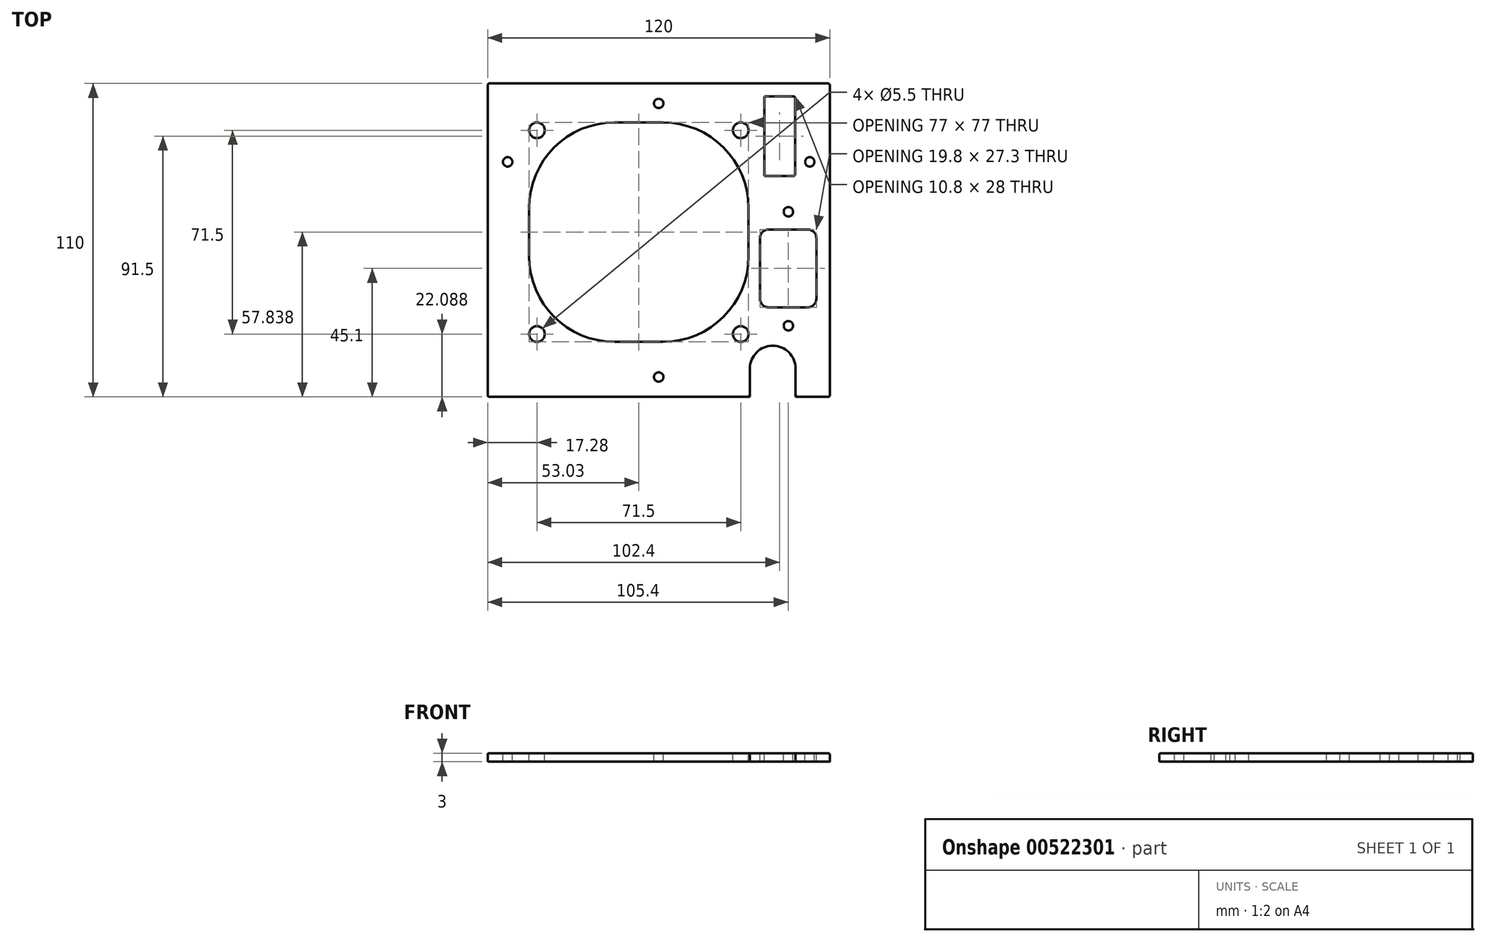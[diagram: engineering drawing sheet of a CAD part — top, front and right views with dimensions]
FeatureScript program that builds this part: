
annotation { "Feature Type Name" : "Feature", "Feature Type Description" : "" }
export const myFeature = defineFeature(function(context is Context, id is Id, definition is map)
    precondition{}
    {
        {
            var Q0;
            Q0=qCreatedBy(makeId("Top.planeOp"),FACE);
            var sketch = newSketch(context, id + "F0", { "sketchPlane" : qUnion([Q0])});
            skLineSegment(sketch, "E0.bottom", {"start": v(-60, 55) * mm, "end": v(60, 55) * mm});
            skLineSegment(sketch, "E0.top", {"start": v(-60, -55) * mm, "end": v(32, -55) * mm});
            skLineSegment(sketch, "E0.left", {"start": v(-60, 55) * mm, "end": v(-60, -55) * mm});
            skLineSegment(sketch, "E0.right", {"start": v(60, 55) * mm, "end": v(60, -55) * mm});
            skArc(sketch, "E1", {"start": v(48, -45) * mm, "mid": v(40, -37) * mm, "end": v(32, -45) * mm});
            skLineSegment(sketch, "E2", {"start": v(48, -45) * mm, "end": v(48, -55) * mm});
            skLineSegment(sketch, "E3", {"start": v(32, -45) * mm, "end": v(32, -55) * mm});
            skLineSegment(sketch, "E4.trimOffspring", {"start": v(48, -55) * mm, "end": v(60, -55) * mm});
            skSolve(sketch);
        }
        {
            var Q0;
            Q0=makeQuery(id+"F0.imprint","IMPRINT",FACE,{"disambiguationData":[TD([[makeQuery(id+"F0.imprint","IMPRINT",EDGE,{"derivedFrom":sQuery(id+"F0.wireOp",EDGE,"E0.bottom")}),-1.0]])]});
            var Q1;
            Q1 = qSketchRegion(id + "F2", true);
            extrude(context, id + "F1", {"entities" : qUnion([Q0, Q1]), "depth" : 3 * mm, "offsetDistance" : 25 * mm});
        }
        {
            var Q0;
            Q0=makeQuery(id+"F1.opExtrude","CAP_FACE",FACE,{"disambiguationData":[OSD([sQuery(id+"F0.wireOp",EDGE,"E0.bottom"),sQuery(id+"F0.wireOp",EDGE,"E0.top"),sQuery(id+"F0.wireOp",EDGE,"E0.left"),sQuery(id+"F0.wireOp",EDGE,"E0.right"),sQuery(id+"F0.wireOp",EDGE,"E1"),sQuery(id+"F0.wireOp",EDGE,"E2"),sQuery(id+"F0.wireOp",EDGE,"E3"),sQuery(id+"F0.wireOp",EDGE,"E4.trimOffspring")])],"isStart":false});
            var sketch = newSketch(context, id + "F2", { "sketchPlane" : qUnion([Q0])});
            skPoint(sketch, "E5", {"position": v(-53, 27.5) * mm});
            skPoint(sketch, "E6", {"position": v(53, 27.5) * mm});
            skPoint(sketch, "E7", {"position": v(0, 48) * mm});
            skPoint(sketch, "E8", {"position": v(0, -48) * mm});
            skSolve(sketch);
        }
        {
            var Q0;
            Q0=sQuery(id+"F2.wireOp",VERTEX,"E5");
            var Q1;
            Q1=sQuery(id+"F2.wireOp",VERTEX,"E7");
            var Q2;
            Q2=sQuery(id+"F2.wireOp",VERTEX,"E6");
            var Q3;
            Q3=sQuery(id+"F2.wireOp",VERTEX,"E8");
            var Q4;
            Q4=makeQuery(id+"F1.opExtrude","SWEPT_BODY",BODY,{"disambiguationData":[OSD([sQuery(id+"F0.wireOp",EDGE,"E0.bottom"),sQuery(id+"F0.wireOp",EDGE,"E0.top"),sQuery(id+"F0.wireOp",EDGE,"E0.left"),sQuery(id+"F0.wireOp",EDGE,"E0.right"),sQuery(id+"F0.wireOp",EDGE,"E1"),sQuery(id+"F0.wireOp",EDGE,"E2"),sQuery(id+"F0.wireOp",EDGE,"E3"),sQuery(id+"F0.wireOp",EDGE,"E4.trimOffspring")])]});
            hole(context, id + "F3", {"style" : HoleStyle.SIMPLE, "endStyle" : HoleEndStyle.THROUGH, "standardTappedOrClearance" : lookupTablePath({ "standard" : "ISO", "fit" : "Normal", "size" : "M3", "type" : "Clearance" }), "standardBlindInLast" : lookupTablePath({ "fit" : "Standard", "standard" : "ISO", "size" : "M3", "type" : "Clearance" }), "holeDiameter" : 3.3 * mm, "isTappedThrough" : true, "tappedDepth" : 12 * mm, "tapClearance" : 3, "locations" : qUnion([Q0, Q1, Q2, Q3]), "scope" : qUnion([Q4])});
        }
        {
            var Q0;
            Q0=makeQuery(id+"F1.opExtrude","CAP_FACE",FACE,{"disambiguationData":[OSD([sQuery(id+"F0.wireOp",EDGE,"E0.bottom"),sQuery(id+"F0.wireOp",EDGE,"E0.top"),sQuery(id+"F0.wireOp",EDGE,"E0.left"),sQuery(id+"F0.wireOp",EDGE,"E0.right"),sQuery(id+"F0.wireOp",EDGE,"E1"),sQuery(id+"F0.wireOp",EDGE,"E2"),sQuery(id+"F0.wireOp",EDGE,"E3"),sQuery(id+"F0.wireOp",EDGE,"E4.trimOffspring")])],"isStart":false});
            var sketch = newSketch(context, id + "F4", { "sketchPlane" : qUnion([Q0])});
            skPoint(sketch, "E9", {"position": v(-42.72, 38.59) * mm});
            skPoint(sketch, "E10", {"position": v(-42.72, -32.91) * mm});
            skPoint(sketch, "E11", {"position": v(28.78, -32.91) * mm});
            skPoint(sketch, "E12", {"position": v(28.78, 38.59) * mm});
            skLineSegment(sketch, "E13.bottom", {"start": v(1.53, 41.34) * mm, "end": v(-15.47, 41.34) * mm});
            skLineSegment(sketch, "E13.top", {"start": v(1.53, -35.66) * mm, "end": v(-15.47, -35.66) * mm});
            skLineSegment(sketch, "E13.left", {"start": v(31.53, 11.34) * mm, "end": v(31.53, -5.66) * mm});
            skLineSegment(sketch, "E13.right", {"start": v(-45.47, 11.34) * mm, "end": v(-45.47, -5.66) * mm});
            skPoint(sketch, "E14.visualSharp", {"position": v(-45.47, 41.34) * mm});
            skArc(sketch, "E14.filletArc", {"start": v(-15.47, 41.34) * mm, "mid": v(-36.68, 32.55) * mm, "end": v(-45.47, 11.34) * mm});
            skPoint(sketch, "E15.visualSharp", {"position": v(31.53, 41.34) * mm});
            skArc(sketch, "E15.filletArc", {"start": v(31.53, 11.34) * mm, "mid": v(22.74, 32.55) * mm, "end": v(1.53, 41.34) * mm});
            skPoint(sketch, "E16.visualSharp", {"position": v(31.53, -35.66) * mm});
            skArc(sketch, "E16.filletArc", {"start": v(1.53, -35.66) * mm, "mid": v(22.74, -26.88) * mm, "end": v(31.53, -5.66) * mm});
            skPoint(sketch, "E17.visualSharp", {"position": v(-45.47, -35.66) * mm});
            skArc(sketch, "E17.filletArc", {"start": v(-45.47, -5.66) * mm, "mid": v(-36.68, -26.88) * mm, "end": v(-15.47, -35.66) * mm});
            skSolve(sketch);
        }
        {
            var Q0;
            Q0=sQuery(id+"F4.wireOp",VERTEX,"E9");
            var Q1;
            Q1=sQuery(id+"F4.wireOp",VERTEX,"E10");
            var Q2;
            Q2=sQuery(id+"F4.wireOp",VERTEX,"E11");
            var Q3;
            Q3=sQuery(id+"F4.wireOp",VERTEX,"E12");
            var Q4;
            Q4=makeQuery(id+"F1.opExtrude","SWEPT_BODY",BODY,{"disambiguationData":[OSD([sQuery(id+"F0.wireOp",EDGE,"E0.bottom"),sQuery(id+"F0.wireOp",EDGE,"E0.top"),sQuery(id+"F0.wireOp",EDGE,"E0.left"),sQuery(id+"F0.wireOp",EDGE,"E0.right"),sQuery(id+"F0.wireOp",EDGE,"E1"),sQuery(id+"F0.wireOp",EDGE,"E2"),sQuery(id+"F0.wireOp",EDGE,"E3"),sQuery(id+"F0.wireOp",EDGE,"E4.trimOffspring")])]});
            hole(context, id + "F5", {"style" : HoleStyle.SIMPLE, "endStyle" : HoleEndStyle.THROUGH, "standardTappedOrClearance" : lookupTablePath({ "standard" : "ISO", "fit" : "Normal", "size" : "M5", "type" : "Clearance" }), "standardBlindInLast" : lookupTablePath({ "fit" : "Standard", "standard" : "ISO", "size" : "M5", "type" : "Clearance" }), "holeDiameter" : 5.5 * mm, "isTappedThrough" : true, "tappedDepth" : 12 * mm, "tapClearance" : 3, "locations" : qUnion([Q0, Q1, Q2, Q3]), "scope" : qUnion([Q4])});
        }
        {
            var Q0;
            Q0 = qSketchRegion(id + "F4", true);
            extrude(context, id + "F6", {"entities" : qUnion([Q0]), "operationType" : NewBodyOperationType.REMOVE, "endBound" : BoundingType.THROUGH_ALL, "oppositeDirection" : true, "depth" : 25 * mm, "offsetDistance" : 25 * mm});
        }
        {
            var Q0;
            Q0=makeQuery(id+"F1.opExtrude","SWEPT_EDGE",EDGE,{"disambiguationData":[OSD([sQuery(id+"F0.wireOp",EDGE,"E0.bottom"),sQuery(id+"F0.wireOp",EDGE,"E0.left")])]});
            var Q1;
            Q1=makeQuery(id+"F1.opExtrude","SWEPT_EDGE",EDGE,{"disambiguationData":[OSD([sQuery(id+"F0.wireOp",EDGE,"E0.bottom"),sQuery(id+"F0.wireOp",EDGE,"E0.right")])]});
            var Q2;
            Q2=makeQuery(id+"F1.opExtrude","SWEPT_EDGE",EDGE,{"disambiguationData":[OSD([sQuery(id+"F0.wireOp",EDGE,"E0.right"),sQuery(id+"F0.wireOp",EDGE,"E4.trimOffspring")])]});
            var Q3;
            Q3=makeQuery(id+"F1.opExtrude","SWEPT_EDGE",EDGE,{"disambiguationData":[OSD([sQuery(id+"F0.wireOp",EDGE,"E0.top"),sQuery(id+"F0.wireOp",EDGE,"E0.left")])]});
            fillet(context, id + "F7", {"entities" : qUnion([Q0, Q1, Q2, Q3]), "radius" : 0.6 * mm, "tangentPropagation" : true, "allowEdgeOverflow" : false});
        }
        {
            var Q0;
            Q0=makeQuery(id+"F1.opExtrude","CAP_EDGE",EDGE,{"disambiguationData":[OSD([sQuery(id+"F0.wireOp",EDGE,"E1")])],"isStart":false});
            var Q1;
            Q1=makeQuery(id+"F1.opExtrude","CAP_EDGE",EDGE,{"disambiguationData":[OSD([sQuery(id+"F0.wireOp",EDGE,"E0.top")])],"isStart":false});
            fillet(context, id + "F8", {"entities" : qUnion([Q0, Q1]), "radius" : 0.5 * mm, "tangentPropagation" : true, "allowEdgeOverflow" : false});
        }
        {
            var Q0;
            Q0=makeQuery(id+"F1.opExtrude","CAP_FACE",FACE,{"disambiguationData":[OSD([sQuery(id+"F0.wireOp",EDGE,"E0.bottom"),sQuery(id+"F0.wireOp",EDGE,"E0.top"),sQuery(id+"F0.wireOp",EDGE,"E0.left"),sQuery(id+"F0.wireOp",EDGE,"E0.right"),sQuery(id+"F0.wireOp",EDGE,"E1"),sQuery(id+"F0.wireOp",EDGE,"E2"),sQuery(id+"F0.wireOp",EDGE,"E3"),sQuery(id+"F0.wireOp",EDGE,"E4.trimOffspring")])],"isStart":false});
            var sketch = newSketch(context, id + "F9", { "sketchPlane" : qUnion([Q0])});
            skPoint(sketch, "E18", {"position": v(45.5, 10) * mm});
            skPoint(sketch, "E19", {"position": v(45.5, -30) * mm});
            skLineSegment(sketch, "E20.bottom", {"start": v(38.5, 3.75) * mm, "end": v(52.3, 3.75) * mm});
            skLineSegment(sketch, "E20.top", {"start": v(38.5, -23.55) * mm, "end": v(52.3, -23.55) * mm});
            skLineSegment(sketch, "E20.left", {"start": v(35.5, 0.75) * mm, "end": v(35.5, -20.55) * mm});
            skLineSegment(sketch, "E20.right", {"start": v(55.3, 0.75) * mm, "end": v(55.3, -20.55) * mm});
            skPoint(sketch, "E21.visualSharp", {"position": v(35.5, -23.55) * mm});
            skArc(sketch, "E21.filletArc", {"start": v(35.5, -20.55) * mm, "mid": v(36.38, -22.67) * mm, "end": v(38.5, -23.55) * mm});
            skPoint(sketch, "E22.visualSharp", {"position": v(35.5, 3.75) * mm});
            skArc(sketch, "E22.filletArc", {"start": v(38.5, 3.75) * mm, "mid": v(36.38, 2.87) * mm, "end": v(35.5, 0.75) * mm});
            skPoint(sketch, "E23.visualSharp", {"position": v(55.3, 3.75) * mm});
            skArc(sketch, "E23.filletArc", {"start": v(55.3, 0.75) * mm, "mid": v(54.42, 2.87) * mm, "end": v(52.3, 3.75) * mm});
            skPoint(sketch, "E24.visualSharp", {"position": v(55.3, -23.55) * mm});
            skArc(sketch, "E24.filletArc", {"start": v(52.3, -23.55) * mm, "mid": v(54.42, -22.67) * mm, "end": v(55.3, -20.55) * mm});
            skPoint(sketch, "E25", {"position": v(0, 0) * mm});
            skSolve(sketch);
        }
        {
            var Q0;
            Q0=sQuery(id+"F9.wireOp",VERTEX,"E18");
            var Q1;
            Q1=sQuery(id+"F9.wireOp",VERTEX,"E19");
            var Q2;
            Q2=makeQuery(id+"F1.opExtrude","SWEPT_BODY",BODY,{"disambiguationData":[OSD([sQuery(id+"F0.wireOp",EDGE,"E0.bottom"),sQuery(id+"F0.wireOp",EDGE,"E0.top"),sQuery(id+"F0.wireOp",EDGE,"E0.left"),sQuery(id+"F0.wireOp",EDGE,"E0.right"),sQuery(id+"F0.wireOp",EDGE,"E1"),sQuery(id+"F0.wireOp",EDGE,"E2"),sQuery(id+"F0.wireOp",EDGE,"E3"),sQuery(id+"F0.wireOp",EDGE,"E4.trimOffspring")])]});
            hole(context, id + "F10", {"style" : HoleStyle.SIMPLE, "endStyle" : HoleEndStyle.THROUGH, "standardTappedOrClearance" : lookupTablePath({ "standard" : "ISO", "fit" : "Normal", "size" : "M3", "type" : "Clearance" }), "standardBlindInLast" : lookupTablePath({ "fit" : "Standard", "standard" : "ISO", "size" : "M3", "type" : "Clearance" }), "holeDiameter" : 3.3 * mm, "isTappedThrough" : true, "tappedDepth" : 12 * mm, "tapClearance" : 3, "locations" : qUnion([Q0, Q1]), "scope" : qUnion([Q2])});
        }
        {
            var Q0;
            Q0 = qSketchRegion(id + "F9", true);
            extrude(context, id + "F11", {"entities" : qUnion([Q0]), "operationType" : NewBodyOperationType.REMOVE, "endBound" : BoundingType.THROUGH_ALL, "oppositeDirection" : true, "depth" : 25 * mm, "offsetDistance" : 25 * mm});
        }
        {
            var Q0;
            Q0=makeQuery(id+"F1.opExtrude","CAP_FACE",FACE,{"disambiguationData":[OSD([sQuery(id+"F0.wireOp",EDGE,"E0.bottom"),sQuery(id+"F0.wireOp",EDGE,"E0.top"),sQuery(id+"F0.wireOp",EDGE,"E0.left"),sQuery(id+"F0.wireOp",EDGE,"E0.right"),sQuery(id+"F0.wireOp",EDGE,"E1"),sQuery(id+"F0.wireOp",EDGE,"E2"),sQuery(id+"F0.wireOp",EDGE,"E3"),sQuery(id+"F0.wireOp",EDGE,"E4.trimOffspring")])],"isStart":false});
            var sketch = newSketch(context, id + "F12", { "sketchPlane" : qUnion([Q0])});
            skLineSegment(sketch, "E26.bottom", {"start": v(37, 50.5) * mm, "end": v(47.8, 50.5) * mm});
            skLineSegment(sketch, "E26.top", {"start": v(37, 22.5) * mm, "end": v(47.8, 22.5) * mm});
            skLineSegment(sketch, "E26.left", {"start": v(37, 50.5) * mm, "end": v(37, 22.5) * mm});
            skLineSegment(sketch, "E26.right", {"start": v(47.8, 50.5) * mm, "end": v(47.8, 22.5) * mm});
            skPoint(sketch, "E27", {"position": v(0, 0) * mm});
            skSolve(sketch);
        }
        {
            var Q0;
            Q0=makeQuery(id+"F12.imprint","IMPRINT",FACE,{"disambiguationData":[TD([[makeQuery(id+"F12.imprint","IMPRINT",EDGE,{"derivedFrom":sQuery(id+"F12.wireOp",EDGE,"E26.bottom")}),-1.0]])]});
            extrude(context, id + "F13", {"entities" : qUnion([Q0]), "operationType" : NewBodyOperationType.REMOVE, "endBound" : BoundingType.THROUGH_ALL, "oppositeDirection" : true, "depth" : 25 * mm, "offsetDistance" : 25 * mm});
        }
        {
            var Q0;
            Q0=makeQuery(id+"F13.boolean.opBoolean","COPY",EDGE,{"derivedFrom":makeQuery(id+"F13.opExtrude","SWEPT_EDGE",EDGE,{"disambiguationData":[OSD([sQuery(id+"F12.wireOp",EDGE,"E26.top"),sQuery(id+"F12.wireOp",EDGE,"E26.left")])]})});
            var Q1;
            Q1=makeQuery(id+"F13.boolean.opBoolean","COPY",EDGE,{"derivedFrom":makeQuery(id+"F13.opExtrude","SWEPT_EDGE",EDGE,{"disambiguationData":[OSD([sQuery(id+"F12.wireOp",EDGE,"E26.bottom"),sQuery(id+"F12.wireOp",EDGE,"E26.left")])]})});
            var Q2;
            Q2=makeQuery(id+"F13.boolean.opBoolean","COPY",EDGE,{"derivedFrom":makeQuery(id+"F13.opExtrude","SWEPT_EDGE",EDGE,{"disambiguationData":[OSD([sQuery(id+"F12.wireOp",EDGE,"E26.bottom"),sQuery(id+"F12.wireOp",EDGE,"E26.right")])]})});
            var Q3;
            Q3=makeQuery(id+"F13.boolean.opBoolean","COPY",EDGE,{"derivedFrom":makeQuery(id+"F13.opExtrude","SWEPT_EDGE",EDGE,{"disambiguationData":[OSD([sQuery(id+"F12.wireOp",EDGE,"E26.top"),sQuery(id+"F12.wireOp",EDGE,"E26.right")])]})});
            fillet(context, id + "F14", {"entities" : qUnion([Q0, Q1, Q2, Q3]), "radius" : 0.5 * mm, "tangentPropagation" : true, "allowEdgeOverflow" : false});
        }
    });
